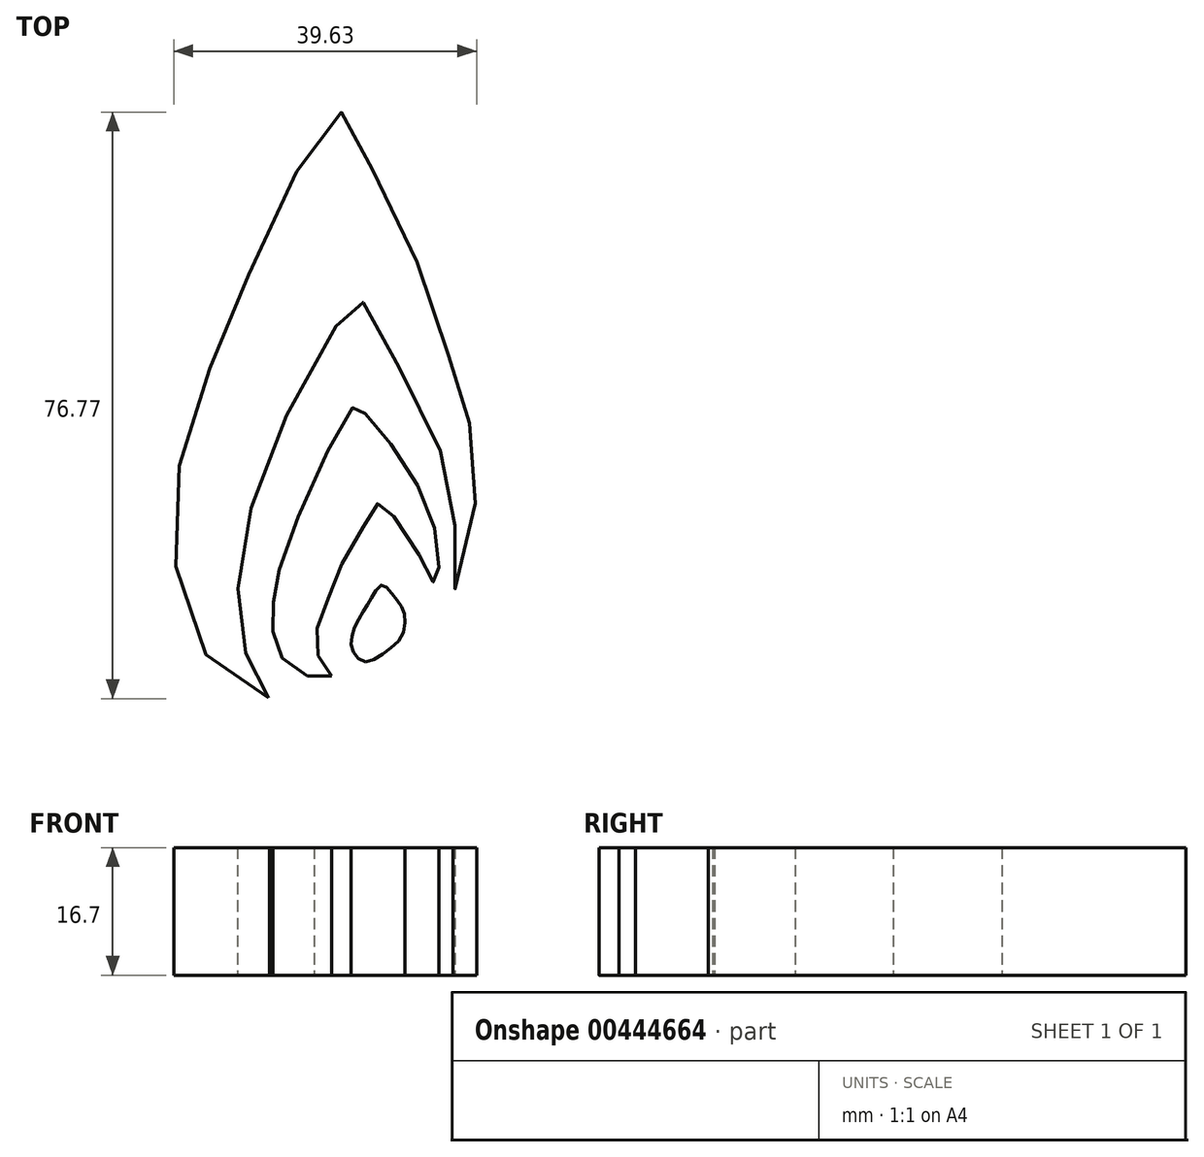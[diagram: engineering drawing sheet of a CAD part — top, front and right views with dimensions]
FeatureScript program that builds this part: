
annotation { "Feature Type Name" : "Feature", "Feature Type Description" : "" }
export const myFeature = defineFeature(function(context is Context, id is Id, definition is map)
    precondition{}
    {
        {
            var Q0;
            Q0=qCreatedBy(makeId("Top.planeOp"),FACE);
            var sketch = newSketch(context, id + "F0", { "sketchPlane" : qUnion([Q0])});
            skFitSpline(sketch, "E0", {"points": [v(-69.76, -36.64) * mm, v(-76.91, -32.17) * mm, v(-81.92, -19.53) * mm, v(-80.96, -3.85) * mm, v(-75.42, 11.35) * mm, v(-68.5, 27.5) * mm, v(-60.93, 39.9) * mm, v(-59.86, 39.72) * mm, v(-56.52, 33.23) * mm, v(-49.49, 18.32) * mm, v(-45.37, 5.27) * mm, v(-43.35, -1.17) * mm, v(-42.81, -11.84) * mm, v(-45.43, -22.4) * mm, v(-45.43, -16.37) * mm, v(-46.15, -7.55) * mm, v(-51.28, 4.02) * mm, v(-56.4, 13.43) * mm, v(-58.31, 16) * mm, v(-59.62, 14.33) * mm, v(-66.42, 2.4) * mm, v(-72.14, -12.14) * mm, v(-73.81, -22.27) * mm, v(-73.27, -29.3) * mm, v(-70.95, -34.08) * mm, v(-69.76, -36.64) * mm]});
            skFitSpline(sketch, "E1", {"points": [v(-61.53, -33.73) * mm, v(-65.35, -33.5) * mm, v(-68.8, -29.8) * mm, v(-69.16, -24.79) * mm, v(-67.43, -16.92) * mm, v(-58.5, 1.68) * mm, v(-57.77, 1.32) * mm, v(-51.81, -6.19) * mm, v(-47.52, -17.63) * mm, v(-48, -21.57) * mm, v(-49.9, -18.23) * mm, v(-55.15, -11.08) * mm, v(-55.75, -11.61) * mm, v(-60.04, -18.83) * mm, v(-62.78, -25.92) * mm, v(-63.56, -30.57) * mm, v(-61.53, -33.73) * mm]});
            skFitSpline(sketch, "E2", {"points": [v(-57.05, -31.92) * mm, v(-54.77, -30.8) * mm, v(-52.45, -28.72) * mm, v(-51.95, -26.09) * mm, v(-52.56, -24.39) * mm, v(-53.84, -22.76) * mm, v(-54.92, -21.83) * mm, v(-56.08, -23.11) * mm, v(-57.05, -24.77) * mm, v(-58.17, -26.63) * mm, v(-58.94, -28.99) * mm, v(-58.6, -30.8) * mm, v(-57.05, -31.92) * mm]});
            skSolve(sketch);
        }
        {
            var Q0;
            Q0 = qSketchRegion(id + "F0", true);
            extrude(context, id + "F1", {"entities" : qUnion([Q0]), "depth" : 16.7 * mm});
        }
    });
